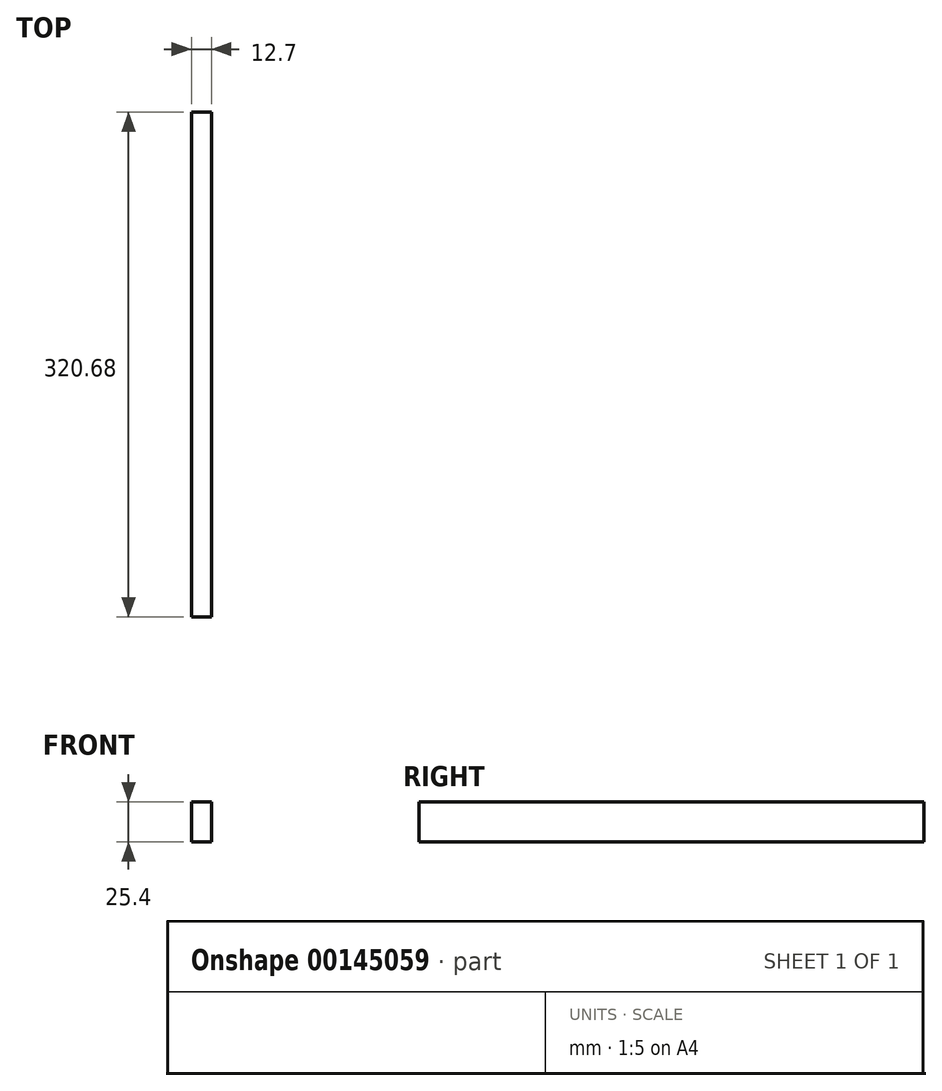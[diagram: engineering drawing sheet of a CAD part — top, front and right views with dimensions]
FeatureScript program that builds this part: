
annotation { "Feature Type Name" : "Feature", "Feature Type Description" : "" }
export const myFeature = defineFeature(function(context is Context, id is Id, definition is map)
    precondition{}
    {
        {
            var Q0;
            Q0=qCreatedBy(makeId("Front.planeOp"),FACE);
            var sketch = newSketch(context, id + "F0", { "sketchPlane" : qUnion([Q0])});
            skLineSegment(sketch, "E0.bottom", {"start": v(0, 0) * mm, "end": v(12.7, 0) * mm});
            skLineSegment(sketch, "E0.top", {"start": v(0, 25.4) * mm, "end": v(12.7, 25.4) * mm});
            skLineSegment(sketch, "E0.left", {"start": v(0, 0) * mm, "end": v(0, 25.4) * mm});
            skLineSegment(sketch, "E0.right", {"start": v(12.7, 0) * mm, "end": v(12.7, 25.4) * mm});
            skSolve(sketch);
        }
        {
            var Q0;
            Q0=makeQuery(id+"F0.imprint","IMPRINT",FACE,{"disambiguationData":[TD([[makeQuery(id+"F0.imprint","IMPRINT",EDGE,{"derivedFrom":sQuery(id+"F0.wireOp",EDGE,"E0.bottom")}),1.0]])]});
            extrude(context, id + "F1", {"entities" : qUnion([Q0]), "depth" : 320.67 * mm});
        }
    });
